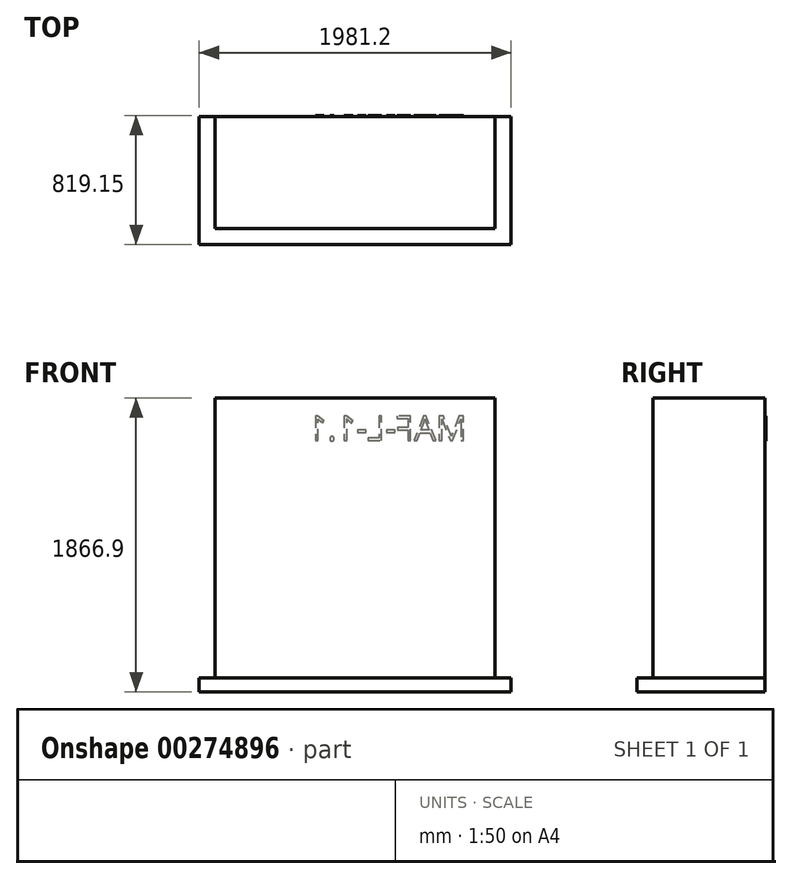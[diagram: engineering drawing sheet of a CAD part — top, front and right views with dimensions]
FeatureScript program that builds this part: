
annotation { "Feature Type Name" : "Feature", "Feature Type Description" : "" }
export const myFeature = defineFeature(function(context is Context, id is Id, definition is map)
    precondition{}
    {
        {
            var Q0;
            Q0=qCreatedBy(makeId("Top.planeOp"),FACE);
            var sketch = newSketch(context, id + "F0", { "sketchPlane" : qUnion([Q0])});
            skLineSegment(sketch, "E0.bottom", {"start": v(0, 0) * mm, "end": v(1778, 0) * mm});
            skLineSegment(sketch, "E0.top", {"start": v(0, 965.2) * mm, "end": v(1778, 965.2) * mm});
            skLineSegment(sketch, "E0.left", {"start": v(0, 0) * mm, "end": v(0, 965.2) * mm});
            skLineSegment(sketch, "E0.right", {"start": v(1778, 0) * mm, "end": v(1778, 965.2) * mm});
            skSolve(sketch);
        }
        {
            var Q0;
            Q0=makeQuery(id+"F0.imprint","IMPRINT",FACE,{"disambiguationData":[TD([[makeQuery(id+"F0.imprint","IMPRINT",EDGE,{"derivedFrom":sQuery(id+"F0.wireOp",EDGE,"E0.bottom")}),1.0]])]});
            extrude(context, id + "F1", {"entities" : qUnion([Q0]), "depth" : 1778 * mm});
        }
        {
            var Q0;
            Q0=makeQuery(id+"F1.opExtrude","SWEPT_FACE",FACE,{"disambiguationData":[OSD([sQuery(id+"F0.wireOp",EDGE,"E0.top")])]});
            var sketch = newSketch(context, id + "F2", { "sketchPlane" : qUnion([Q0])});
            skText(sketch, "E1", { "text": "MAF-L-1.1", "fontName": "OpenSans-Regular.ttf"});
            const initialGuessF2  = {"E1": [-1.59793, 1.50746, 1, 0, 0.15747]};
            skSetInitialGuess(sketch, initialGuessF2);
            skSolve(sketch);
        }
        {
            var Q0;
            Q0 = qSketchRegion(id + "F2", true);
            extrude(context, id + "F3", {"entities" : qUnion([Q0]), "operationType" : NewBodyOperationType.ADD, "depth" : 6.35 * mm});
        }
        {
            var Q0;
            Q0=makeQuery(id+"F1.opExtrude","SWEPT_FACE",FACE,{"disambiguationData":[OSD([sQuery(id+"F0.wireOp",EDGE,"E0.bottom")])]});
            extrude(context, id + "F4", {"entities" : qUnion([Q0]), "operationType" : NewBodyOperationType.REMOVE, "oppositeDirection" : true, "depth" : 254 * mm});
        }
        {
            var Q0;
            Q0=makeQuery(id+"F1.opExtrude","CAP_FACE",FACE,{"disambiguationData":[OSD([sQuery(id+"F0.wireOp",EDGE,"E0.bottom"),sQuery(id+"F0.wireOp",EDGE,"E0.top"),sQuery(id+"F0.wireOp",EDGE,"E0.left"),sQuery(id+"F0.wireOp",EDGE,"E0.right")])],"isStart":true});
            extrude(context, id + "F5", {"entities" : qUnion([Q0]), "operationType" : NewBodyOperationType.ADD, "depth" : 88.9 * mm});
        }
        {
            var Q0;
            {var subQ0=sQuery(id+"F0.wireOp",EDGE,"E0.bottom");Q0=makeQuery(id+"F5.boolean.opBoolean","MERGE",FACE,{"derivedFrom":[makeQuery(id+"F4.boolean.opBoolean","COPY",FACE,{"derivedFrom":makeQuery(id+"F4.opExtrude","CAP_FACE",FACE,{"disambiguationData":[OSD([subQ0])],"isStart":false})}),makeQuery(id+"F5.opExtrude","SWEPT_FACE",FACE,{"disambiguationData":[OSD([subQ0])]})]});}
            var sketch = newSketch(context, id + "F6", { "sketchPlane" : qUnion([Q0])});
            skLineSegment(sketch, "E2.bottom", {"start": v(0, -88.9) * mm, "end": v(1778, -88.9) * mm});
            skLineSegment(sketch, "E2.top", {"start": v(0, 0) * mm, "end": v(1778, 0) * mm});
            skLineSegment(sketch, "E2.left", {"start": v(0, -88.9) * mm, "end": v(0, 0) * mm});
            skLineSegment(sketch, "E2.right", {"start": v(1778, -88.9) * mm, "end": v(1778, 0) * mm});
            skSolve(sketch);
        }
        {
            var Q0;
            Q0=makeQuery(id+"F6.imprint","IMPRINT",FACE,{"disambiguationData":[TD([[makeQuery(id+"F6.imprint","IMPRINT",EDGE,{"derivedFrom":sQuery(id+"F6.wireOp",EDGE,"E2.bottom")}),1.0]])]});
            extrude(context, id + "F7", {"entities" : qUnion([Q0]), "operationType" : NewBodyOperationType.ADD, "depth" : 101.6 * mm});
        }
        {
            var Q0;
            {var subQ0=sQuery(id+"F0.wireOp",EDGE,"E0.left");Q0=makeQuery(id+"F7.boolean.opBoolean","MERGE",FACE,{"derivedFrom":[makeQuery(id+"F5.boolean.opBoolean","MERGE",FACE,{"derivedFrom":[makeQuery(id+"F1.opExtrude","SWEPT_FACE",FACE,{"disambiguationData":[OSD([subQ0])]}),makeQuery(id+"F5.opExtrude","SWEPT_FACE",FACE,{"disambiguationData":[OSD([subQ0])]})]}),makeQuery(id+"F7.opExtrude","SWEPT_FACE",FACE,{"disambiguationData":[OSD([sQuery(id+"F6.wireOp",EDGE,"E2.left")])]})]});}
            var sketch = newSketch(context, id + "F8", { "sketchPlane" : qUnion([Q0])});
            skLineSegment(sketch, "E3.bottom", {"start": v(-152.4, 0) * mm, "end": v(-965.2, 0) * mm});
            skLineSegment(sketch, "E3.top", {"start": v(-152.4, -88.9) * mm, "end": v(-965.2, -88.9) * mm});
            skLineSegment(sketch, "E3.left", {"start": v(-152.4, 0) * mm, "end": v(-152.4, -88.9) * mm});
            skLineSegment(sketch, "E3.right", {"start": v(-965.2, 0) * mm, "end": v(-965.2, -88.9) * mm});
            skSolve(sketch);
        }
        {
            var Q0;
            Q0=makeQuery(id+"F8.imprint","IMPRINT",FACE,{"disambiguationData":[TD([[makeQuery(id+"F8.imprint","IMPRINT",EDGE,{"derivedFrom":sQuery(id+"F8.wireOp",EDGE,"E3.top")}),-1.0]])]});
            extrude(context, id + "F9", {"entities" : qUnion([Q0]), "operationType" : NewBodyOperationType.ADD, "depth" : 101.6 * mm});
        }
        {
            var Q0;
            {var subQ0=sQuery(id+"F0.wireOp",EDGE,"E0.right");Q0=makeQuery(id+"F7.boolean.opBoolean","MERGE",FACE,{"derivedFrom":[makeQuery(id+"F5.boolean.opBoolean","MERGE",FACE,{"derivedFrom":[makeQuery(id+"F1.opExtrude","SWEPT_FACE",FACE,{"disambiguationData":[OSD([subQ0])]}),makeQuery(id+"F5.opExtrude","SWEPT_FACE",FACE,{"disambiguationData":[OSD([subQ0])]})]}),makeQuery(id+"F7.opExtrude","SWEPT_FACE",FACE,{"disambiguationData":[OSD([sQuery(id+"F6.wireOp",EDGE,"E2.right")])]})]});}
            var sketch = newSketch(context, id + "F10", { "sketchPlane" : qUnion([Q0])});
            skLineSegment(sketch, "E4.bottom", {"start": v(152.4, 0) * mm, "end": v(965.2, 0) * mm});
            skLineSegment(sketch, "E4.top", {"start": v(152.4, -88.9) * mm, "end": v(965.2, -88.9) * mm});
            skLineSegment(sketch, "E4.left", {"start": v(152.4, 0) * mm, "end": v(152.4, -88.9) * mm});
            skLineSegment(sketch, "E4.right", {"start": v(965.2, 0) * mm, "end": v(965.2, -88.9) * mm});
            skSolve(sketch);
        }
        {
            var Q0;
            Q0=makeQuery(id+"F10.imprint","IMPRINT",FACE,{"disambiguationData":[TD([[makeQuery(id+"F10.imprint","IMPRINT",EDGE,{"derivedFrom":sQuery(id+"F10.wireOp",EDGE,"E4.top")}),1.0]])]});
            extrude(context, id + "F11", {"entities" : qUnion([Q0]), "operationType" : NewBodyOperationType.ADD, "depth" : 101.6 * mm});
        }
    });
